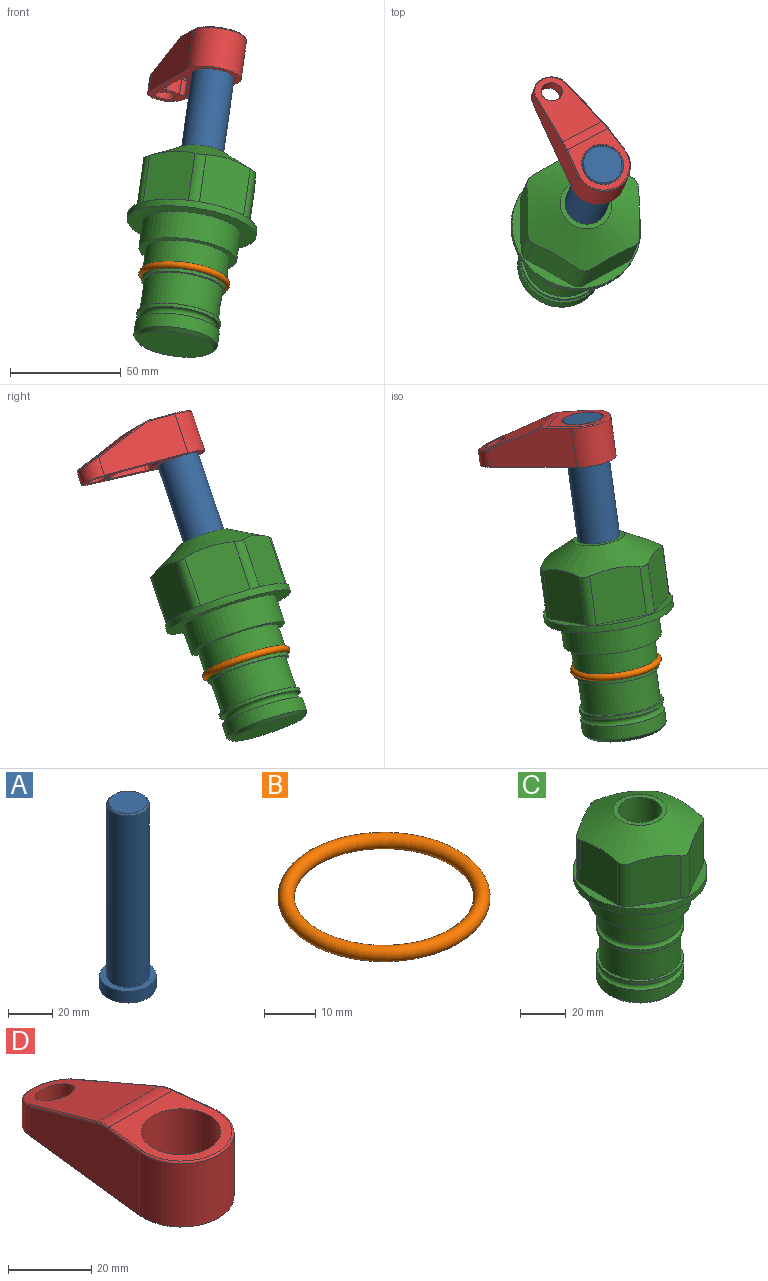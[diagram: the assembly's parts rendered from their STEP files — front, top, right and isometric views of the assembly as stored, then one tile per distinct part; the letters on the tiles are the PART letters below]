
ASSEMBLY  parts=4 mates=2
PART A: 6 faces, bbox 25.4x25.4x101.6 mm
  f0: plane 17.46x17.46mm, normal (0,0,1), area 239.5mm2, adj f5
  f1: plane 25.4x25.4mm, normal (0,0,-1), area 506.7mm2, adj f2
  f2: cylinder r=12.7mm len=25.4mm, axis (0,0,1), area 506.7mm2, adj f1,f3
  f3: plane 25.4x25.4mm, normal (0,0,1), area 221.7mm2, adj f2,f4
  f4: cylinder r=9.53mm len=94.46mm, axis (0,0,1), area 5653mm2, adj f3,f5
  f5: cone r=8.73mm half-angle=45deg, axis (0,0,-1), area 64.4mm2, adj f0,f4
PART B: 1 faces, bbox 44.7x44.7x3.2 mm
  f0: torus R=19.05mm, axis (0,0,1), area 1193.9mm2
PART C: 36 faces, bbox 58.7x58.7x91.2 mm
  f0: cylinder r=17.78mm len=35.56mm, axis (0,0,1), area 1670.8mm2, adj f23,f24,f31
  f1: cylinder r=19.05mm len=38.1mm, axis (0,0,1), area 1191.9mm2, adj f26,f27,f30
  f2: plane 58.66x58.66mm, normal (0,0,-1), area 1150.6mm2, adj f3,f28
  f3: cylinder r=29.33mm len=58.66mm, axis (0,0,-1), area 585.1mm2, adj f2,f4
  f4: plane 58.66x58.66mm, normal (0,0,1), area 475.9mm2, adj f3,f5,f6,f7,f8,f9,f10,f11
  f5: plane 24.5x20.32mm, normal (-0.5,0.87,0), area 562.8mm2, adj f4,f15,f16,f17
  f6: plane 24.5x20.32mm, normal (0.5,0.87,0), area 562.8mm2, adj f4,f14,f15,f17
  f7: plane 24.5x23.48mm, normal (1,0,0), area 562.8mm2, adj f4,f13,f14,f17
  f8: plane 24.5x20.32mm, normal (0.5,-0.87,0), area 562.8mm2, adj f4,f12,f13,f17
  f9: plane 24.5x20.32mm, normal (-0.5,-0.87,0), area 562.8mm2, adj f4,f11,f12,f17
  f10: plane 24.5x23.48mm, normal (-1,0,0), area 562.8mm2, adj f4,f11,f16,f17
  f11: cylinder r=5.08mm len=23.01mm, axis (0,0,-1), area 121.2mm2, adj f4,f9,f10,f17
  f12: cylinder r=5.08mm len=23.01mm, axis (0,0,-1), area 121.2mm2, adj f4,f8,f9,f17
  f13: cylinder r=5.08mm len=23.01mm, axis (0,0,-1), area 121.2mm2, adj f4,f7,f8,f17
  f14: cylinder r=5.08mm len=23.01mm, axis (0,0,-1), area 121.2mm2, adj f4,f6,f7,f17
  f15: cylinder r=5.08mm len=23.01mm, axis (0,0,-1), area 121.2mm2, adj f4,f5,f6,f17
  f16: cylinder r=5.08mm len=23.01mm, axis (0,0,-1), area 121.2mm2, adj f4,f5,f10,f17
  f17: cone r=11.73mm half-angle=60deg, axis (0,0,-1), area 2071.8mm2, adj f5,f6,f7,f8,f9,f10,f11,f12
  f18: plane 23.46x23.46mm, normal (0,0,1), area 147.4mm2, adj f17,f35
  f19: plane 34.93x34.93mm, normal (0,0,-1), area 958mm2, adj f29
  f20: cylinder r=19.05mm len=38.1mm, axis (0,0,1), area 760.1mm2, adj f21,f29
  f21: torus R=19.05mm, axis (0,0,1), area 565.3mm2, adj f20,f22
  f22: cylinder r=19.05mm len=38.1mm, axis (0,0,1), area 190mm2, adj f21,f23
  f23: plane 38.1x38.1mm, normal (0,0,1), area 146.9mm2, adj f0,f22
  f24: plane 38.1x38.1mm, normal (0,0,-1), area 146.9mm2, adj f0,f25
  f25: cylinder r=19.05mm len=38.1mm, axis (0,0,1), area 190mm2, adj f24,f26
  f26: torus R=19.05mm, axis (0,0,1), area 565.3mm2, adj f1,f25
  f27: plane 44.45x44.45mm, normal (0,0,-1), area 411.7mm2, adj f1,f28
  f28: cylinder r=22.23mm len=44.45mm, axis (0,0,1), area 1773.5mm2, adj f2,f27
  f29: cone r=19.05mm half-angle=45deg, axis (0,0,1), area 257.5mm2, adj f19,f20
  f30: cylinder r=3.17mm len=6.75mm, axis (-1,0,0), area 128mm2, adj f1,f33
  f31: cylinder r=3.17mm len=6.35mm, axis (-1,0,0), area 102.5mm2, adj f0,f33
  f32: plane 25.4x25.4mm, normal (0,0,1), area 506.7mm2, adj f33
  f33: cylinder r=12.7mm len=66.42mm, axis (0,0,-1), area 5236.2mm2, adj f30,f31,f32,f34
  f34: cone r=9.53mm half-angle=30deg, axis (0,0,-1), area 443.4mm2, adj f33,f35
  f35: cylinder r=9.53mm len=19.05mm, axis (0,0,-1), area 849mm2, adj f18,f34
PART D: 44 faces, bbox 27.5x64.5x19.1 mm
  f0: plane 2.3x0.95mm, normal (0,0,-1), area 1mm2, adj f25,f30,f34
  f1: plane 63.5x25.4mm, normal (0,0,-1), area 561.7mm2, adj f2,f3,f4,f5,f6,f7,f19,f20
  f2: cylinder r=12.7mm len=25.4mm, axis (0,0,-1), area 792.2mm2, adj f1,f3,f5,f13
  f3: plane 42.33x18.54mm, normal (0.99,0.11,0), area 647mm2, adj f1,f2,f4,f11,f12,f14
  f4: cylinder r=7.94mm len=15.78mm, axis (0,0,-1), area 158.6mm2, adj f1,f3,f5,f16
  f5: plane 42.33x18.54mm, normal (-0.99,0.11,0), area 647mm2, adj f1,f2,f4,f15,f17,f18
  f6: cylinder r=9.53mm len=19.05mm, axis (0,0,-1), area 1140.1mm2, adj f1,f8
  f7: cylinder r=4.76mm len=10.98mm, axis (0,0,-1), area 276.1mm2, adj f1,f9
  f8: plane 25.83x24.38mm, normal (0,0,1), area 262.2mm2, adj f6,f10,f11,f13,f15
  f9: plane 32.49x20.55mm, normal (0,0.34,0.94), area 489.9mm2, adj f7,f10,f14,f16,f18
  f10: cylinder r=12.7mm len=21.49mm, axis (-1,0,0), area 93.2mm2, adj f8,f9,f12,f17
  f11: cylinder r=0.51mm len=12.34mm, axis (0.11,-0.99,0), area 9.9mm2, adj f3,f8,f12,f13
  f12: bspline ~7.62x1.64mm, area 3.5mm2, adj f3,f10,f11,f14
  f13: torus R=12.19mm, axis (0,0,1), area 33.6mm2, adj f2,f8,f11,f15
  f14: cylinder r=0.51mm len=26.01mm, axis (0.1,-0.93,0.34), area 21.6mm2, adj f3,f9,f12,f16
  f15: cylinder r=0.51mm len=12.34mm, axis (0.11,0.99,0), area 9.9mm2, adj f5,f8,f13,f17
  f16: bspline ~15.78x7.05mm, area 15.7mm2, adj f4,f9,f14,f18
  f17: bspline ~7.62x1.64mm, area 3.5mm2, adj f5,f10,f15,f18
  f18: cylinder r=0.51mm len=26.01mm, axis (0.1,0.93,-0.34), area 21.6mm2, adj f5,f9,f16,f17
  f19: plane 21.6x14.29mm, normal (-0.99,-0.11,0), area 242.6mm2, adj f1,f26,f28,f34,f36,f38
  f20: plane 21.6x14.29mm, normal (0.99,-0.11,0), area 242.6mm2, adj f1,f27,f29,f37,f39,f41
  f21: cylinder r=12.7mm len=14.29mm, axis (0,0,-1), area 173.2mm2, adj f1,f26,f27,f30,f31,f33
  f22: cylinder r=7.94mm len=7.63mm, axis (0,0,-1), area 53.8mm2, adj f1,f28,f29,f42
  f23: plane 2.3x0.95mm, normal (0,0,-1), area 1mm2, adj f25,f33,f37
  f24: plane 17.94x12.32mm, normal (0,-0.34,-0.94), area 191.2mm2, adj f25,f38,f41,f42
  f25: cylinder r=9.53mm len=12.93mm, axis (-1,0,0), area 37.5mm2, adj f0,f23,f24,f31,f36,f39
  f26: cylinder r=1.59mm len=14.29mm, axis (0,0,-1), area 49mm2, adj f1,f19,f21,f32
  f27: cylinder r=1.59mm len=14.29mm, axis (0,0,-1), area 49mm2, adj f1,f20,f21,f35
  f28: cylinder r=1.59mm len=7.28mm, axis (0,0,-1), area 22.1mm2, adj f1,f19,f22,f40
  f29: cylinder r=1.59mm len=7.28mm, axis (0,0,-1), area 22.1mm2, adj f1,f20,f22,f43
  f30: torus R=14.29mm, axis (0,0,1), area 5.8mm2, adj f0,f21,f31,f32
  f31: bspline ~11.06x2.73mm, area 20.8mm2, adj f21,f25,f30,f33
  f32: sphere r=1.59mm, area 5.4mm2, adj f26,f30,f34
  f33: torus R=14.29mm, axis (0,0,1), area 5.8mm2, adj f21,f23,f31,f35
  f34: cylinder r=1.59mm len=1.68mm, axis (-0.11,0.99,0), area 2.4mm2, adj f0,f19,f32,f36
  f35: sphere r=1.59mm, area 5.4mm2, adj f27,f33,f37
  f36: bspline ~5.82x2.33mm, area 7.7mm2, adj f19,f25,f34,f38
  f37: cylinder r=1.59mm len=1.68mm, axis (0.11,0.99,0), area 2.4mm2, adj f20,f23,f35,f39
  f38: cylinder r=1.59mm len=18.33mm, axis (0.1,-0.93,0.34), area 46.7mm2, adj f19,f24,f36,f40
  f39: bspline ~5.82x2.33mm, area 7.7mm2, adj f20,f25,f37,f41
  f40: sphere r=1.59mm, area 3.6mm2, adj f28,f38,f42
  f41: cylinder r=1.59mm len=18.33mm, axis (0.1,0.93,-0.34), area 46.7mm2, adj f20,f24,f39,f43
  f42: bspline ~8.31x1.84mm, area 15.3mm2, adj f22,f24,f40,f43
  f43: sphere r=1.59mm, area 3.6mm2, adj f29,f41,f42
PLACE A rot(axis=(-0.45,0.35,0.82),35.4deg) t=(13.13,-57.52,18.98)mm
PLACE B rot(axis=(-0.92,0.39,0),20deg) t=(10.68,-63.31,1.69)mm
PLACE C rot(axis=(-0.92,0.39,0),20deg) t=(10.68,-63.31,1.69)mm
PLACE D rot(axis=(-0.45,0.35,0.82),35.4deg) t=(20.41,-40.33,70.3)mm
MATE cylindrical A.f2 <-> C.f0  axis (0.13,0.31,0.94) through (16.55,-49.45,43.08)mm
MATE fastened D.f2 <-> A.f2  axis (-0.13,-0.31,-0.94) through (22.95,-34.34,88.21)mm
